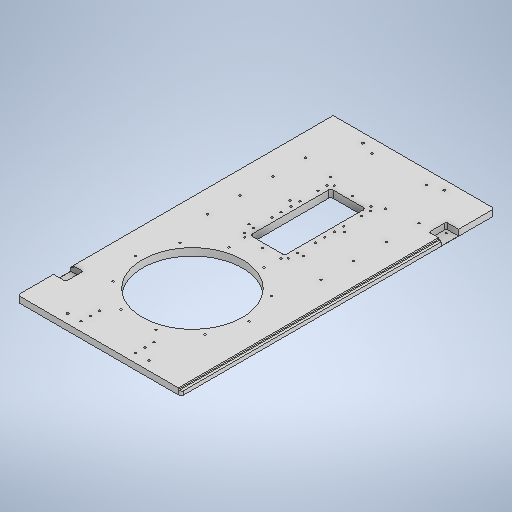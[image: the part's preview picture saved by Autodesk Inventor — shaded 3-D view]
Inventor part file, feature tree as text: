
AUTODESK INVENTOR PART (.ipt)
format: ipt  version: 2025 (Build 290162000, 162)  size: 553,472 bytes
history: native  units: in
note: dims shown in document units (in); Inventor stores cm internally (conversion verified against a paired STEP export)
features: sketch x17, extrude x6, hole x5, fillet x3, chamfer x3, plane x2
ambient origin geometry x8: Origin, YZ Plane, XZ Plane, XY Plane, X Axis, Y Axis, Z Axis, Center Point
bodies: Solid1 (feature_tree)
feature tree (36):
  extrude  "Base Cover"  Depth=27.1654in
  sketch  "Sketch2"  dims[d5=8.6614in d6=0.0in d7=0.0in]
  extrude  "Cylinder Hole"  Depth=0.6299in
  plane  "Work Plane1"
  hole  "Hole3"  [1 undecoded]
  sketch  "Sketch7"  dims[d69=0.1575in d70=3.937in d72=360.0deg]
  plane  "Work Plane2"
  hole  "Hole4"  [1 undecoded]
  sketch  "Sketch9"  dims[d82=1.063in]
  fillet  "Rounded Side Corners"  Radius=7.0625in
  chamfer  "Chamfer1"  Distance=3.937in Angle=360.0deg
  chamfer  "Chamfer2"  Distance=0.1969in
  extrude  "Magnet Seats"  Depth=0.3937in TaperAngle=45.0deg
  hole  "Hole5"  [1 undecoded]
  chamfer  "Chamfer5"  Distance=0.1181in
  hole  "Hole6"  [1 undecoded]
  sketch  "Sketch15"  dims[d85=1.4961in]
  extrude  "Extrusion11"  Depth=0.3937in TaperAngle=0.0deg
  fillet  "Fillet3"  Radius=0.748in
  hole  "Hole7"  [1 undecoded]
  fillet  "Rounded Bottom Corners"  Radius=0.8661in
  extrude  "Side Rail_L"  Depth=0.3937in
  extrude  "Side Rail_R"  Depth=0.3937in
  sketch  "Sketch1"  dims[d0=14.1732in d1=27.1654in]
  sketch  "Sketch6"  dims[d68=9.8425in]
  sketch  "Sketch8"  dims[d74=0.1628in d75=0.3937in d76=0.1575in d77=0.0787in d78=90.0deg d79=0.3937in d80=0.8108in]
  sketch  "Sketch Circular Pattern4"  dims[d57=0.1936in d58=0.1969in d59=0.1575in d60=0.0787in d61=90.0deg d62=0.1969in d63=0.8108in]
  sketch  "Sketch11"  dims[d83=1.063in]
  sketch  "Sketch12"  dims[d84=1.4961in]
  sketch  "Sketch Rectangular Pattern1"  dims[d2=0.6299in d3=0.0in d4=8.0709in]
  sketch  "Sketch Rectangular Pattern2"  dims[d8=10.6299in d50=5.9055in d55=7.0625in]
  sketch  "Sketch Rectangular Pattern3"  dims[d56=25.5906in]
  sketch  "Sketch Rectangular Pattern4"  dims[d64=10.3543in]
  sketch  "Sketch Rectangular Pattern5"  dims[d65=10.6299in]
  sketch  "Sketch16"  dims[d86=3.1102in]
  sketch  "Sketch17"  dims[d87=3.1102in d88=0.1969in d89=0.0984in d90=0.0787in d91=45.0deg d92=0.0984in d93=0.0787in d94=45.0deg d95=0.1181in d96=0.1181in d97=0.5118in d98=0.0in d109=0.748in d110=0.315in d111=0.8661in d112=0.748in d113=0.1299in d114=0.1299in d115=0.1299in d116=0.1299in d118=0.315in d119=0.8661in d120=0.748in d121=0.748in d122=0.1276in d123=0.315in d124=0.1575in d125=0.0787in d126=90.0deg d127=0.315in d128=0.8108in d129=0.0138in d130=0.0787in d131=45.0deg d146=3.9469in d147=0.7874in d148=0.3937in d149=0.1575in d150=3.937in d152=1.1811in d153=0.3937in d155=0.3937in d157=0.1575in d158=1.1811in d160=0.7874in d161=0.3937in d163=0.3937in d165=9.8425in d166=0.1575in d167=2.9528in d168=1.1811in d169=3.1496in d171=1.4173in d172=0.3937in d174=0.3937in d176=0.1628in d177=0.3937in d178=0.1575in d179=0.0787in d180=90.0deg d181=0.3937in d182=0.8108in d191=3.0in d192=7.0in d193=6.4961in d194=0.8312in d195=0.0in d196=0.1969in d197=0.3937in d198=0.1969in d199=1.9685in d201=0.7874in d202=0.3937in d204=0.3937in d206=0.3189in d207=0.1969in d208=0.3189in d209=1.9685in d211=0.7874in d212=0.3937in d214=0.3937in d216=0.1628in d217=0.3937in d218=0.1575in d219=0.0787in d220=90.0deg d221=0.3937in d222=0.8108in d230=0.2756in d231=0.2362in d232=0.0787in d233=0.1378in d234=0.503in d235=0.5906in d236=0.0in d237=0.1378in d238=0.0787in d239=0.2362in d240=0.503in d241=0.3937in d242=0.0in d26=0.0394in d27=0.0394in d28=0.0394in d29=0.0059in d30=0.0098in d31=0.0148in d32=0.5635in d33=0.0295in d34=0.8108in d35=0.0025in d36=0.0295in d37=0.0148in d66=0.0197in d67=0.0344in]
note: 5 required parameter values undecoded (feature->parameter linkage not recoverable at this tier; creation-order binding heuristic only, values carry confidence <= 0.55)
